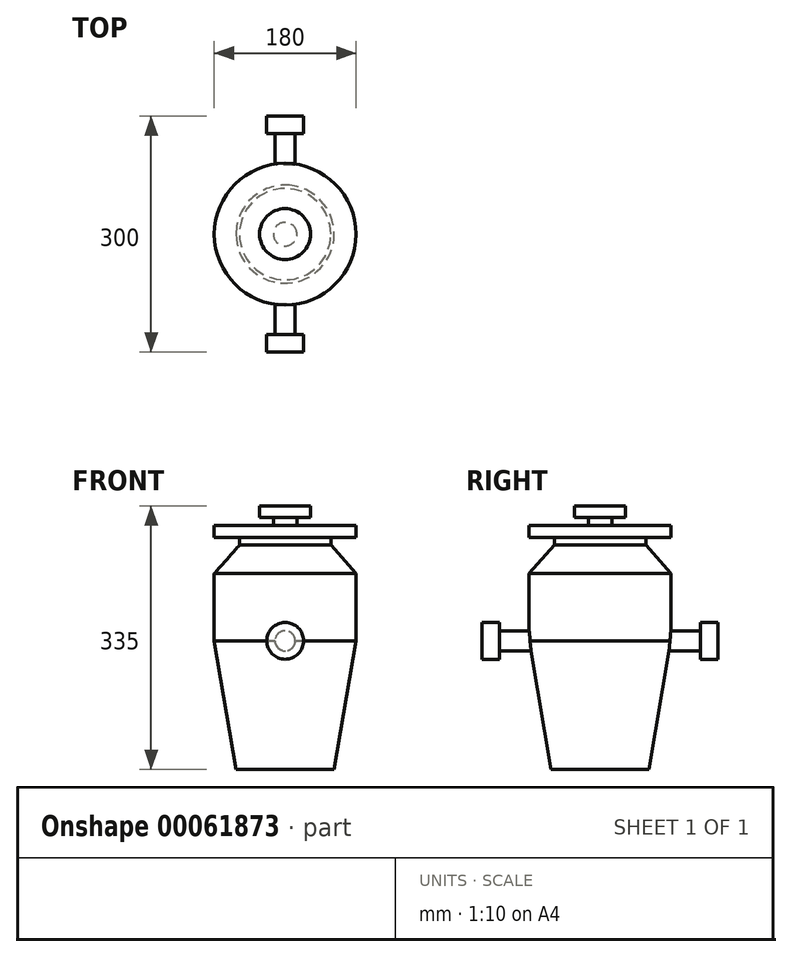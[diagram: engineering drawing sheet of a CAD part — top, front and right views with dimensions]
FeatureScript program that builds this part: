
annotation { "Feature Type Name" : "Feature", "Feature Type Description" : "" }
export const myFeature = defineFeature(function(context is Context, id is Id, definition is map)
    precondition{}
    {
        {
            var Q0;
            Q0=qCreatedBy(makeId("Front.planeOp"),FACE);
            var sketch = newSketch(context, id + "F0", { "sketchPlane" : qUnion([Q0])});
            skLineSegment(sketch, "E0", {"start": v(0, 0) * mm, "end": v(0, 171.67) * mm});
            skLineSegment(sketch, "E1", {"start": v(0, 171.67) * mm, "end": v(32.35, 171.67) * mm});
            skLineSegment(sketch, "E2", {"start": v(32.35, 171.67) * mm, "end": v(32.35, 156.67) * mm});
            skLineSegment(sketch, "E3", {"start": v(32.35, 156.67) * mm, "end": v(15, 156.67) * mm});
            skLineSegment(sketch, "E4", {"start": v(15, 156.67) * mm, "end": v(15, 146.67) * mm});
            skLineSegment(sketch, "E5", {"start": v(15, 146.67) * mm, "end": v(90, 146.67) * mm});
            skLineSegment(sketch, "E6", {"start": v(90, 146.67) * mm, "end": v(90, 131.67) * mm});
            skLineSegment(sketch, "E7", {"start": v(90, 131.67) * mm, "end": v(58.03, 131.67) * mm});
            skLineSegment(sketch, "E8", {"start": v(58.03, 131.67) * mm, "end": v(58.03, 121.67) * mm});
            skLineSegment(sketch, "E9", {"start": v(58.03, 121.67) * mm, "end": v(90, 85.4) * mm});
            skLineSegment(sketch, "E10", {"start": v(90, 85.4) * mm, "end": v(90, 0) * mm});
            skLineSegment(sketch, "E11", {"start": v(90, 0) * mm, "end": v(62.31, -163.33) * mm});
            skLineSegment(sketch, "E12", {"start": v(62.31, -163.33) * mm, "end": v(0, -163.33) * mm});
            skLineSegment(sketch, "E13", {"start": v(0, -163.33) * mm, "end": v(0, 0) * mm});
            skSolve(sketch);
        }
        {
            var Q0;
            Q0 = qSketchRegion(id + "F0", true);
            var Q1;
            Q1=sQuery(id+"F0.wireOp",EDGE,"E0");
            revolve(context, id + "F1", {"entities" : qUnion([Q0]), "axis" : qUnion([Q1]), "revolveType" : RevolveType.FULL});
        }
        {
            var Q0;
            Q0=qCreatedBy(makeId("Right.planeOp"),FACE);
            var sketch = newSketch(context, id + "F2", { "sketchPlane" : qUnion([Q0])});
            skLineSegment(sketch, "E14", {"start": v(0, 0) * mm, "end": v(-127.71, 0) * mm});
            skLineSegment(sketch, "E15", {"start": v(-127.71, -23.34) * mm, "end": v(-150, -23.34) * mm});
            skLineSegment(sketch, "E16", {"start": v(-150, -23.34) * mm, "end": v(-150, 0) * mm});
            skLineSegment(sketch, "E17", {"start": v(-150, 0) * mm, "end": v(-127.71, 0) * mm});
            skLineSegment(sketch, "E18", {"start": v(-127.71, -23.34) * mm, "end": v(-127.71, -12.82) * mm});
            skLineSegment(sketch, "E19", {"start": v(-127.71, -12.82) * mm, "end": v(0, -12.82) * mm});
            skLineSegment(sketch, "E20", {"start": v(0, -12.82) * mm, "end": v(0, 0) * mm});
            skSolve(sketch);
        }
        {
            var Q0;
            Q0=makeQuery(id+"F2.imprint","IMPRINT",FACE,{"disambiguationData":[TD([[makeQuery(id+"F2.imprint","IMPRINT",EDGE,{"derivedFrom":sQuery(id+"F2.wireOp",EDGE,"E14")}),1.0]])]});
            var Q1;
            Q1=sQuery(id+"F2.wireOp",EDGE,"E14");
            revolve(context, id + "F3", {"entities" : qUnion([Q0]), "axis" : qUnion([Q1]), "revolveType" : RevolveType.FULL});
        }
        {
            var Q0;
            Q0=makeQuery(id+"F3.opRevolve","SWEPT_BODY",BODY,{"disambiguationData":[OSD([sQuery(id+"F2.wireOp",EDGE,"E14"),sQuery(id+"F2.wireOp",EDGE,"E15"),sQuery(id+"F2.wireOp",EDGE,"E16"),sQuery(id+"F2.wireOp",EDGE,"E17"),sQuery(id+"F2.wireOp",EDGE,"E18"),sQuery(id+"F2.wireOp",EDGE,"E19"),sQuery(id+"F2.wireOp",EDGE,"E20")])]});
            var Q1;
            Q1=qCreatedBy(makeId("Front.planeOp"),FACE);
            mirror(context, id + "F4", {"operationType" : NewBodyOperationType.ADD, "entities" : qUnion([Q0]), "mirrorPlane" : qUnion([Q1])});
        }
    });
